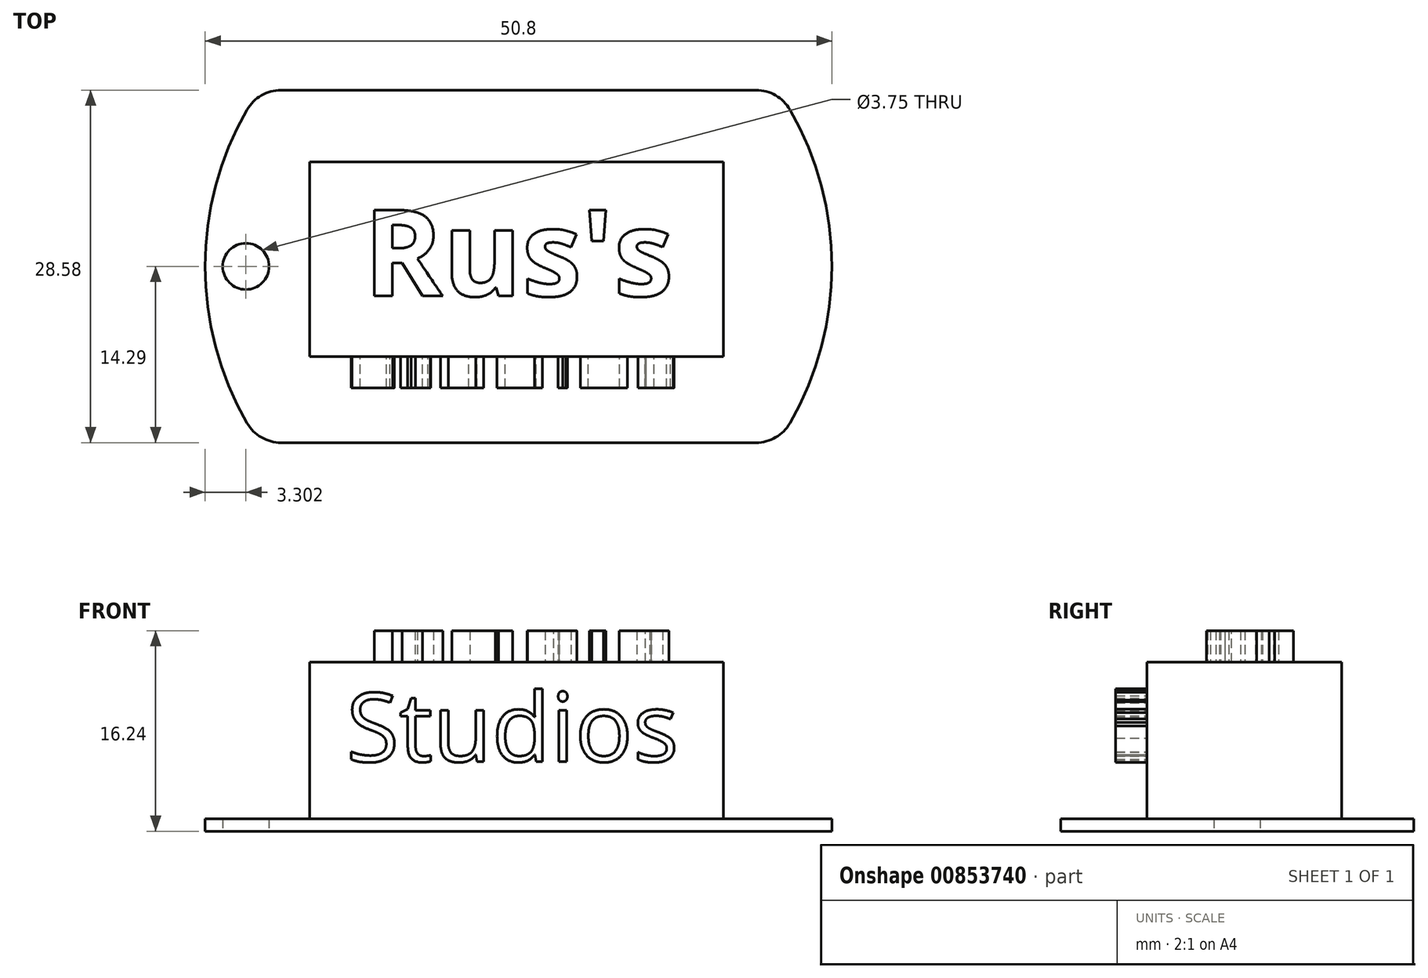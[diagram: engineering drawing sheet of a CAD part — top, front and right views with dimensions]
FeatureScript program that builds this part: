
annotation { "Feature Type Name" : "Feature", "Feature Type Description" : "" }
export const myFeature = defineFeature(function(context is Context, id is Id, definition is map)
    precondition{}
    {
        {
            var Q0;
            Q0=qCreatedBy(makeId("Top.planeOp"),FACE);
            var sketch = newSketch(context, id + "F0", { "sketchPlane" : qUnion([Q0])});
            skArc(sketch, "E0", {"start": v(-22, 12.7) * mm, "mid": v(-25.4, 0) * mm, "end": v(-22, -12.7) * mm});
            skLineSegment(sketch, "E1.top", {"start": v(-19.25, -14.29) * mm, "end": v(19.25, -14.29) * mm});
            skArc(sketch, "E2.trimOffspring", {"start": v(22, -12.7) * mm, "mid": v(25.4, 0) * mm, "end": v(22, 12.7) * mm});
            skLineSegment(sketch, "E3", {"start": v(-19.25, 14.29) * mm, "end": v(19.25, 14.29) * mm});
            skPoint(sketch, "E4.visualSharp", {"position": v(-21, 14.29) * mm});
            skArc(sketch, "E4.filletArc", {"start": v(-19.25, 14.29) * mm, "mid": v(-20.83, 13.86) * mm, "end": v(-22, 12.7) * mm});
            skPoint(sketch, "E5.visualSharp", {"position": v(21, 14.29) * mm});
            skArc(sketch, "E5.filletArc", {"start": v(22, 12.7) * mm, "mid": v(20.83, 13.86) * mm, "end": v(19.25, 14.29) * mm});
            skPoint(sketch, "E6.visualSharp", {"position": v(21, -14.29) * mm});
            skArc(sketch, "E6.filletArc", {"start": v(19.25, -14.29) * mm, "mid": v(20.83, -13.86) * mm, "end": v(22, -12.7) * mm});
            skPoint(sketch, "E7.visualSharp", {"position": v(-21, -14.29) * mm});
            skArc(sketch, "E7.filletArc", {"start": v(-22, -12.7) * mm, "mid": v(-20.83, -13.86) * mm, "end": v(-19.25, -14.29) * mm});
            skCircle(sketch, "E8", {"center": v(-22.1, 0) * mm, "radius": 1.87 * mm});
            skSolve(sketch);
        }
        {
            var Q0;
            Q0=makeQuery(id+"F0.imprint","IMPRINT",FACE,{"disambiguationData":[TD([[makeQuery(id+"F0.imprint","IMPRINT",EDGE,{"derivedFrom":sQuery(id+"F0.wireOp",EDGE,"E0")}),1.0]])]});
            extrude(context, id + "F1", {"entities" : qUnion([Q0]), "depth" : 1 * mm, "offsetDistance" : 25.4 * mm});
        }
        {
            var Q0;
            Q0=makeQuery(id+"F1.opExtrude","CAP_FACE",FACE,{"disambiguationData":[OSD([sQuery(id+"F0.wireOp",EDGE,"E0"),sQuery(id+"F0.wireOp",EDGE,"E1.top"),sQuery(id+"F0.wireOp",EDGE,"E2.trimOffspring"),sQuery(id+"F0.wireOp",EDGE,"E3"),sQuery(id+"F0.wireOp",EDGE,"E4.filletArc"),sQuery(id+"F0.wireOp",EDGE,"E5.filletArc"),sQuery(id+"F0.wireOp",EDGE,"E6.filletArc"),sQuery(id+"F0.wireOp",EDGE,"E7.filletArc"),sQuery(id+"F0.wireOp",EDGE,"E8")])],"isStart":false});
            var sketch = newSketch(context, id + "F2", { "sketchPlane" : qUnion([Q0])});
            skLineSegment(sketch, "E9.bottom", {"start": v(-16.91, 8.47) * mm, "end": v(16.6, 8.47) * mm});
            skLineSegment(sketch, "E9.top", {"start": v(-16.91, -7.3) * mm, "end": v(16.6, -7.3) * mm});
            skLineSegment(sketch, "E9.left", {"start": v(-16.91, 8.47) * mm, "end": v(-16.91, -7.3) * mm});
            skLineSegment(sketch, "E9.right", {"start": v(16.6, 8.47) * mm, "end": v(16.6, -7.3) * mm});
            skSolve(sketch);
        }
        {
            var Q0;
            Q0=makeQuery(id+"F2.imprint","IMPRINT",FACE,{"disambiguationData":[TD([[makeQuery(id+"F2.imprint","IMPRINT",EDGE,{"derivedFrom":sQuery(id+"F2.wireOp",EDGE,"E9.bottom")}),-1.0]])]});
            extrude(context, id + "F3", {"entities" : qUnion([Q0]), "depth" : 12.7 * mm, "offsetDistance" : 25.4 * mm});
        }
        {
            var Q0;
            Q0=makeQuery(id+"F3.opExtrude","CAP_FACE",FACE,{"disambiguationData":[OSD([sQuery(id+"F2.wireOp",EDGE,"E9.bottom"),sQuery(id+"F2.wireOp",EDGE,"E9.top"),sQuery(id+"F2.wireOp",EDGE,"E9.left"),sQuery(id+"F2.wireOp",EDGE,"E9.right")])],"isStart":false});
            var sketch = newSketch(context, id + "F4", { "sketchPlane" : qUnion([Q0])});
            skText(sketch, "E10", { "text": "Rus\'s", "fontName": "OpenSans-Bold.ttf"});
            const initialGuessF4  = {"E10": [-0.01258, -0.0024, 1, 0, 0.00702]};
            skSetInitialGuess(sketch, initialGuessF4);
            skSolve(sketch);
        }
        {
            var Q0;
            Q0 = qSketchRegion(id + "F4", true);
            extrude(context, id + "F5", {"entities" : qUnion([Q0]), "operationType" : NewBodyOperationType.ADD, "depth" : 2.54 * mm, "offsetDistance" : 25.4 * mm});
        }
        {
            var Q0;
            Q0=makeQuery(id+"F3.opExtrude","SWEPT_FACE",FACE,{"disambiguationData":[OSD([sQuery(id+"F2.wireOp",EDGE,"E9.top")])]});
            var sketch = newSketch(context, id + "F6", { "sketchPlane" : qUnion([Q0])});
            skText(sketch, "E11", { "text": "Studios", "fontName": "OpenSans-Regular.ttf"});
            const initialGuessF6  = {"E11": [-0.01396, 0.00564, 1, 0, 0.0056]};
            skSetInitialGuess(sketch, initialGuessF6);
            skSolve(sketch);
        }
        {
            var Q0;
            Q0 = qSketchRegion(id + "F6", true);
            extrude(context, id + "F7", {"entities" : qUnion([Q0]), "operationType" : NewBodyOperationType.ADD, "depth" : 2.54 * mm, "offsetDistance" : 25.4 * mm});
        }
    });
